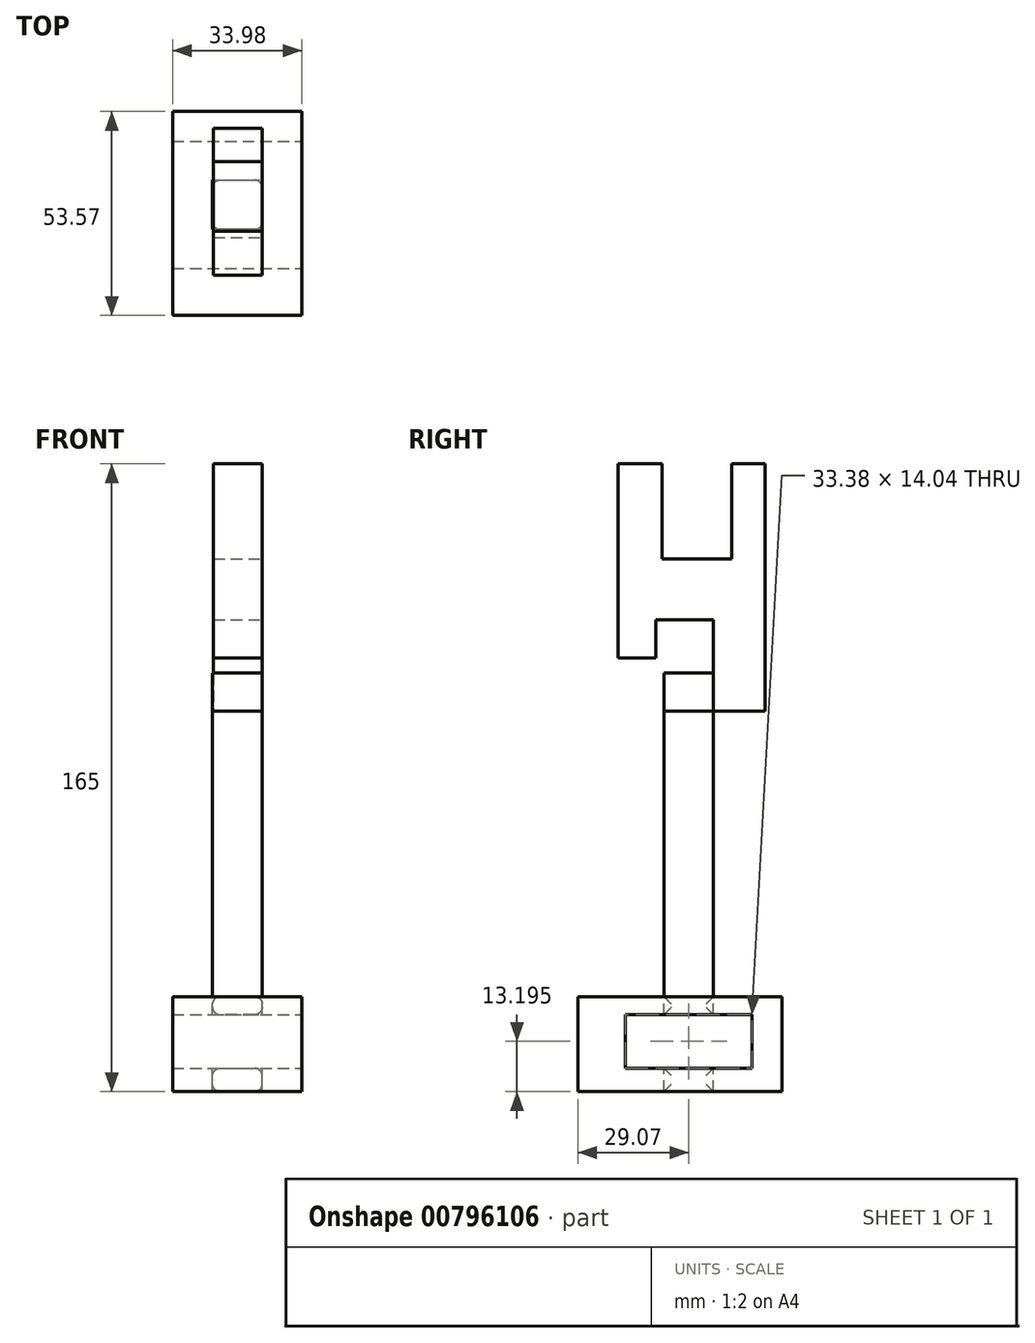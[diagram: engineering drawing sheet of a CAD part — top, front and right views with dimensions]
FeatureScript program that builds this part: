
annotation { "Feature Type Name" : "Feature", "Feature Type Description" : "" }
export const myFeature = defineFeature(function(context is Context, id is Id, definition is map)
    precondition{}
    {
        {
            var Q0;
            Q0=qCreatedBy(makeId("Top.planeOp"),FACE);
            var sketch = newSketch(context, id + "F0", { "sketchPlane" : qUnion([Q0])});
            skCircle(sketch, "E0.cCircle", {"center": v(0, 0) * mm, "radius": 6.51 * mm, "construction": true});
            skLineSegment(sketch, "E0.0", {"start": v(-6.51, 6.51) * mm, "end": v(6.51, 6.51) * mm});
            skLineSegment(sketch, "E0.1", {"start": v(6.51, 6.51) * mm, "end": v(6.51, -6.51) * mm});
            skLineSegment(sketch, "E0.2", {"start": v(6.51, -6.51) * mm, "end": v(-6.51, -6.51) * mm});
            skLineSegment(sketch, "E0.3", {"start": v(-6.51, -6.51) * mm, "end": v(-6.51, 6.51) * mm});
            skPoint(sketch, "E0.0.midPoint", {"position": v(0, 6.51) * mm});
            skSolve(sketch);
        }
        {
            var Q0;
            Q0=makeQuery(id+"F0.imprint","IMPRINT",FACE,{"disambiguationData":[TD([[makeQuery(id+"F0.imprint","IMPRINT",EDGE,{"derivedFrom":sQuery(id+"F0.wireOp",EDGE,"E0.0")}),-1.0]])]});
            extrude(context, id + "F1", {"entities" : qUnion([Q0]), "depth" : 75 * mm, "offsetDistance" : 25 * mm});
        }
        {
            var Q0;
            Q0=makeQuery(id+"F1.opExtrude","CAP_FACE",FACE,{"disambiguationData":[OSD([sQuery(id+"F0.wireOp",EDGE,"E0.0"),sQuery(id+"F0.wireOp",EDGE,"E0.1"),sQuery(id+"F0.wireOp",EDGE,"E0.2"),sQuery(id+"F0.wireOp",EDGE,"E0.3")])],"isStart":true});
            var sketch = newSketch(context, id + "F2", { "sketchPlane" : qUnion([Q0])});
            skLineSegment(sketch, "E1.bottom", {"start": v(17, -24.5) * mm, "end": v(-17, -24.5) * mm});
            skLineSegment(sketch, "E1.top", {"start": v(17, 29.07) * mm, "end": v(-17, 29.07) * mm});
            skLineSegment(sketch, "E1.left", {"start": v(17, -24.5) * mm, "end": v(17, 29.07) * mm});
            skLineSegment(sketch, "E1.right", {"start": v(-17, -24.5) * mm, "end": v(-17, 29.07) * mm});
            skPoint(sketch, "E1.middle", {"position": v(0, 2.29) * mm});
            skSolve(sketch);
        }
        {
            var Q0;
            Q0=makeQuery(id+"F2.imprint","IMPRINT",FACE,{"disambiguationData":[TD([[makeQuery(id+"F2.imprint","IMPRINT",EDGE,{"derivedFrom":sQuery(id+"F2.wireOp",EDGE,"E1.bottom")}),-1.0]])]});
            extrude(context, id + "F3", {"entities" : qUnion([Q0]), "depth" : 25 * mm, "offsetDistance" : 25 * mm});
        }
        {
            var Q0;
            Q0=makeQuery(id+"F1.opExtrude","CAP_FACE",FACE,{"disambiguationData":[OSD([sQuery(id+"F0.wireOp",EDGE,"E0.0"),sQuery(id+"F0.wireOp",EDGE,"E0.1"),sQuery(id+"F0.wireOp",EDGE,"E0.2"),sQuery(id+"F0.wireOp",EDGE,"E0.3")])],"isStart":true});
            extrude(context, id + "F4", {"entities" : qUnion([Q0]), "depth" : 25 * mm, "offsetDistance" : 25 * mm});
        }
        {
            var Q0;
            Q0=makeQuery(id+"F3.opExtrude","SWEPT_FACE",FACE,{"disambiguationData":[OSD([sQuery(id+"F2.wireOp",EDGE,"E1.left")])]});
            var sketch = newSketch(context, id + "F5", { "sketchPlane" : qUnion([Q0])});
            skLineSegment(sketch, "E2.bottom", {"start": v(-16.69, -18.82) * mm, "end": v(16.69, -18.82) * mm});
            skLineSegment(sketch, "E2.top", {"start": v(-16.69, -4.79) * mm, "end": v(16.69, -4.79) * mm});
            skLineSegment(sketch, "E2.left", {"start": v(-16.69, -18.82) * mm, "end": v(-16.69, -4.79) * mm});
            skLineSegment(sketch, "E2.right", {"start": v(16.69, -18.82) * mm, "end": v(16.69, -4.79) * mm});
            skPoint(sketch, "E2.middle", {"position": v(0, -11.8) * mm});
            skSolve(sketch);
        }
        {
            var Q0;
            Q0=makeQuery(id+"F5.imprint","IMPRINT",FACE,{"disambiguationData":[TD([[makeQuery(id+"F5.imprint","IMPRINT",EDGE,{"derivedFrom":sQuery(id+"F5.wireOp",EDGE,"E2.bottom")}),1.0]])]});
            extrude(context, id + "F6", {"entities" : qUnion([Q0]), "operationType" : NewBodyOperationType.REMOVE, "oppositeDirection" : true, "depth" : 34 * mm, "offsetDistance" : 25 * mm});
        }
        {
            var Q0;
            Q0=makeQuery(id+"F1.opExtrude","CAP_FACE",FACE,{"disambiguationData":[OSD([sQuery(id+"F0.wireOp",EDGE,"E0.0"),sQuery(id+"F0.wireOp",EDGE,"E0.1"),sQuery(id+"F0.wireOp",EDGE,"E0.2"),sQuery(id+"F0.wireOp",EDGE,"E0.3")])],"isStart":false});
            var sketch = newSketch(context, id + "F7", { "sketchPlane" : qUnion([Q0])});
            skLineSegment(sketch, "E3.bottom", {"start": v(6.51, 20.1) * mm, "end": v(-6.26, 20.1) * mm});
            skLineSegment(sketch, "E3.top", {"start": v(6.51, -7.07) * mm, "end": v(-6.26, -7.07) * mm});
            skLineSegment(sketch, "E3.left", {"start": v(6.51, 20.1) * mm, "end": v(6.51, -7.07) * mm});
            skLineSegment(sketch, "E3.right", {"start": v(-6.26, 20.1) * mm, "end": v(-6.26, -7.07) * mm});
            skPoint(sketch, "E3.middle", {"position": v(0.13, 6.51) * mm});
            skSolve(sketch);
        }
        {
            var Q0;
            {var subQ0=sQuery(id+"F7.wireOp",EDGE,"E3.bottom");Q0=makeQuery(id+"F7.imprint","IMPRINT",FACE,{"disambiguationData":[TD([[makeQuery(id+"F7.imprint","IMPRINT",EDGE,{"derivedFrom":subQ0}),1.0]])]});}
            extrude(context, id + "F8", {"entities" : qUnion([Q0]), "depth" : 25 * mm, "offsetDistance" : 25 * mm});
        }
        {
            var Q0;
            Q0=makeQuery(id+"F1.opExtrude","CAP_FACE",FACE,{"disambiguationData":[OSD([sQuery(id+"F0.wireOp",EDGE,"E0.0"),sQuery(id+"F0.wireOp",EDGE,"E0.1"),sQuery(id+"F0.wireOp",EDGE,"E0.2"),sQuery(id+"F0.wireOp",EDGE,"E0.3")])],"isStart":false});
            extrude(context, id + "F9", {"entities" : qUnion([Q0]), "depth" : 10 * mm, "offsetDistance" : 25 * mm});
        }
        {
            var Q0;
            Q0=makeQuery(id+"F8.opExtrude","CAP_FACE",FACE,{"disambiguationData":[OSD([sQuery(id+"F0.wireOp",EDGE,"E0.0"),sQuery(id+"F7.wireOp",EDGE,"E3.bottom"),sQuery(id+"F7.wireOp",EDGE,"E3.left"),sQuery(id+"F7.wireOp",EDGE,"E3.right")])],"isStart":false});
            extrude(context, id + "F10", {"entities" : qUnion([Q0]), "operationType" : NewBodyOperationType.ADD, "depth" : 15 * mm, "offsetDistance" : 25 * mm});
        }
        {
            var Q0;
            {var subQ0=sQuery(id+"F0.wireOp",EDGE,"E0.0");Q0=makeQuery(id+"F10.boolean.opBoolean","MERGE",FACE,{"derivedFrom":[makeQuery(id+"F8.opExtrude","SWEPT_FACE",FACE,{"disambiguationData":[OSD([subQ0])]}),makeQuery(id+"F10.opExtrude","SWEPT_FACE",FACE,{"disambiguationData":[OSD([subQ0])]})]});}
            var sketch = newSketch(context, id + "F11", { "sketchPlane" : qUnion([Q0])});
            skLineSegment(sketch, "E4.bottom", {"start": v(-6.26, 98.95) * mm, "end": v(6.51, 98.95) * mm});
            skLineSegment(sketch, "E4.top", {"start": v(-6.26, 115.19) * mm, "end": v(6.51, 115.19) * mm});
            skLineSegment(sketch, "E4.left", {"start": v(-6.26, 98.95) * mm, "end": v(-6.26, 115.19) * mm});
            skLineSegment(sketch, "E4.right", {"start": v(6.51, 98.95) * mm, "end": v(6.51, 115.19) * mm});
            skPoint(sketch, "E4.middle", {"position": v(0.13, 107.07) * mm});
            skPoint(sketch, "E4.middle.positionSnap0", {"position": v(0.13, 115) * mm});
            skPoint(sketch, "E4.centerSnap0", {"position": v(0.13, 115) * mm});
            skSolve(sketch);
        }
        {
            var Q0;
            {var subQ0=sQuery(id+"F11.wireOp",EDGE,"E4.bottom");Q0=makeQuery(id+"F11.imprint","IMPRINT",FACE,{"disambiguationData":[TD([[makeQuery(id+"F11.imprint","IMPRINT",EDGE,{"derivedFrom":subQ0}),1.0]])]});}
            extrude(context, id + "F12", {"entities" : qUnion([Q0]), "operationType" : NewBodyOperationType.ADD, "depth" : 25 * mm, "offsetDistance" : 25 * mm});
        }
        {
            var Q0;
            Q0=makeQuery(id+"F12.opExtrude","SWEPT_FACE",FACE,{"disambiguationData":[OSD([sQuery(id+"F11.wireOp",EDGE,"E4.bottom")])]});
            var sketch = newSketch(context, id + "F13", { "sketchPlane" : qUnion([Q0])});
            skLineSegment(sketch, "E5.bottom", {"start": v(-6.26, 8.67) * mm, "end": v(6.51, 8.67) * mm});
            skLineSegment(sketch, "E5.top", {"start": v(-6.26, 18.49) * mm, "end": v(6.51, 18.49) * mm});
            skLineSegment(sketch, "E5.left", {"start": v(-6.26, 8.67) * mm, "end": v(-6.26, 18.49) * mm});
            skLineSegment(sketch, "E5.right", {"start": v(6.51, 8.67) * mm, "end": v(6.51, 18.49) * mm});
            skSolve(sketch);
        }
        {
            var Q0;
            Q0=makeQuery(id+"F13.imprint","IMPRINT",FACE,{"disambiguationData":[TD([[makeQuery(id+"F13.imprint","IMPRINT",EDGE,{"derivedFrom":sQuery(id+"F13.wireOp",EDGE,"E5.bottom")}),1.0]])]});
            extrude(context, id + "F14", {"entities" : qUnion([Q0]), "operationType" : NewBodyOperationType.ADD, "depth" : 10 * mm, "offsetDistance" : 25 * mm});
        }
        {
            var Q0;
            {var subQ0=sQuery(id+"F0.wireOp",EDGE,"E0.0");Q0=makeQuery(id+"F12.boolean.opBoolean","MERGE",FACE,{"derivedFrom":[makeQuery(id+"F10.opExtrude","CAP_FACE",FACE,{"disambiguationData":[OSD([subQ0,sQuery(id+"F7.wireOp",EDGE,"E3.bottom"),sQuery(id+"F7.wireOp",EDGE,"E3.left"),sQuery(id+"F7.wireOp",EDGE,"E3.right")])],"isStart":false}),makeQuery(id+"F12.opExtrude","SWEPT_FACE",FACE,{"disambiguationData":[OSD([subQ0])]})]});}
            var sketch = newSketch(context, id + "F15", { "sketchPlane" : qUnion([Q0])});
            skLineSegment(sketch, "E6.bottom", {"start": v(6.51, -7) * mm, "end": v(-6.26, -7) * mm});
            skLineSegment(sketch, "E6.top", {"start": v(6.51, -18.49) * mm, "end": v(-6.26, -18.49) * mm});
            skLineSegment(sketch, "E6.left", {"start": v(6.51, -7) * mm, "end": v(6.51, -18.49) * mm});
            skLineSegment(sketch, "E6.right", {"start": v(-6.26, -7) * mm, "end": v(-6.26, -18.49) * mm});
            skSolve(sketch);
        }
        {
            var Q0;
            Q0=makeQuery(id+"F15.imprint","IMPRINT",FACE,{"disambiguationData":[TD([[makeQuery(id+"F15.imprint","IMPRINT",EDGE,{"derivedFrom":sQuery(id+"F15.wireOp",EDGE,"E6.bottom")}),1.0]])]});
            extrude(context, id + "F16", {"entities" : qUnion([Q0]), "operationType" : NewBodyOperationType.ADD, "depth" : 25 * mm, "offsetDistance" : 25 * mm});
        }
        {
            var Q0;
            {var subQ0=sQuery(id+"F0.wireOp",EDGE,"E0.0");Q0=makeQuery(id+"F12.boolean.opBoolean","MERGE",FACE,{"derivedFrom":[makeQuery(id+"F10.opExtrude","CAP_FACE",FACE,{"disambiguationData":[OSD([subQ0,sQuery(id+"F7.wireOp",EDGE,"E3.bottom"),sQuery(id+"F7.wireOp",EDGE,"E3.left"),sQuery(id+"F7.wireOp",EDGE,"E3.right")])],"isStart":false}),makeQuery(id+"F12.opExtrude","SWEPT_FACE",FACE,{"disambiguationData":[OSD([subQ0])]})]});}
            var sketch = newSketch(context, id + "F17", { "sketchPlane" : qUnion([Q0])});
            skLineSegment(sketch, "E7.bottom", {"start": v(-6.26, 11.33) * mm, "end": v(6.51, 11.33) * mm});
            skLineSegment(sketch, "E7.top", {"start": v(-6.26, 20.1) * mm, "end": v(6.51, 20.1) * mm});
            skLineSegment(sketch, "E7.left", {"start": v(-6.26, 11.33) * mm, "end": v(-6.26, 20.1) * mm});
            skLineSegment(sketch, "E7.right", {"start": v(6.51, 11.33) * mm, "end": v(6.51, 20.1) * mm});
            skSolve(sketch);
        }
        {
            var Q0;
            Q0=makeQuery(id+"F17.imprint","IMPRINT",FACE,{"disambiguationData":[TD([[makeQuery(id+"F17.imprint","IMPRINT",EDGE,{"derivedFrom":sQuery(id+"F17.wireOp",EDGE,"E7.bottom")}),1.0]])]});
            extrude(context, id + "F18", {"entities" : qUnion([Q0]), "operationType" : NewBodyOperationType.ADD, "depth" : 25 * mm, "offsetDistance" : 25 * mm});
        }
        {
            var Q0;
            Q0=makeQuery(id+"F4.opExtrude","SWEPT_FACE",FACE,{"disambiguationData":[OSD([sQuery(id+"F0.wireOp",EDGE,"E0.1")])]});
            fillet(context, id + "F19", {"entities" : qUnion([Q0]), "radius" : 2 * mm, "tangentPropagation" : true, "allowEdgeOverflow" : false});
        }
        {
            var Q0;
            Q0=makeQuery(id+"F4.opExtrude","SWEPT_FACE",FACE,{"disambiguationData":[OSD([sQuery(id+"F0.wireOp",EDGE,"E0.3")])]});
            fillet(context, id + "F20", {"entities" : qUnion([Q0]), "radius" : 2 * mm, "tangentPropagation" : true, "allowEdgeOverflow" : false});
        }
    });
